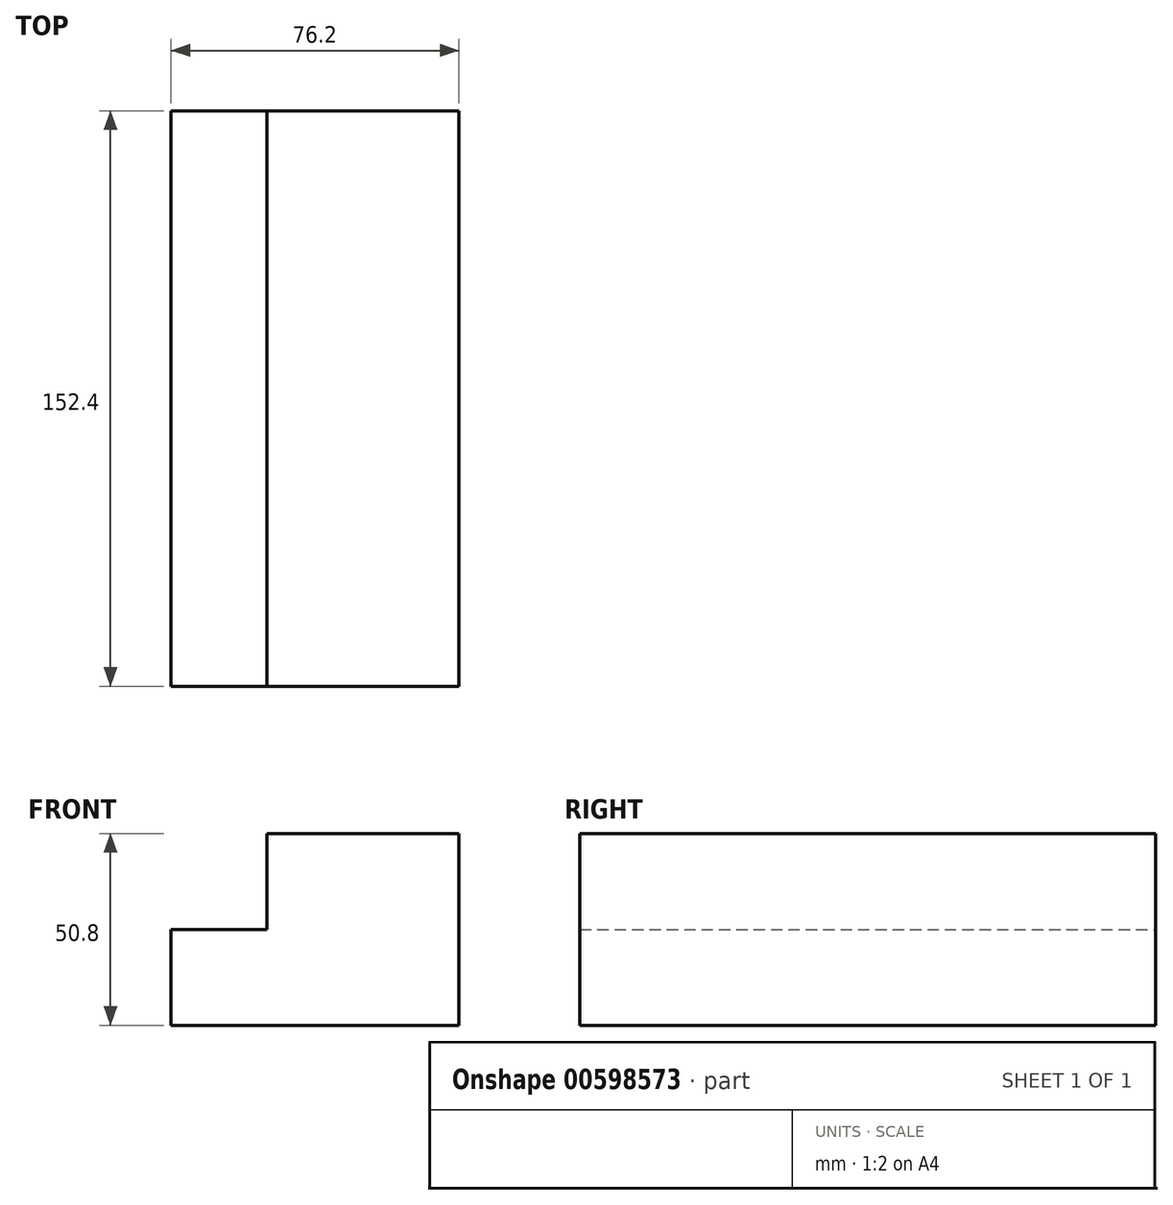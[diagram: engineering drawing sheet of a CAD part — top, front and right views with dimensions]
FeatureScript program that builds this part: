
annotation { "Feature Type Name" : "Feature", "Feature Type Description" : "" }
export const myFeature = defineFeature(function(context is Context, id is Id, definition is map)
    precondition{}
    {
        {
            var Q0;
            Q0=qCreatedBy(makeId("Front.planeOp"),FACE);
            var sketch = newSketch(context, id + "F0", { "sketchPlane" : qUnion([Q0])});
            skLineSegment(sketch, "E0", {"start": v(0, 0) * mm, "end": v(0, 50.8) * mm});
            skLineSegment(sketch, "E1", {"start": v(0, 50.8) * mm, "end": v(-50.8, 50.8) * mm});
            skLineSegment(sketch, "E2", {"start": v(0, 0) * mm, "end": v(-76.2, 0) * mm});
            skLineSegment(sketch, "E3", {"start": v(-76.2, 0) * mm, "end": v(-76.2, 25.4) * mm});
            skLineSegment(sketch, "E4", {"start": v(-76.2, 25.4) * mm, "end": v(-50.8, 25.4) * mm});
            skLineSegment(sketch, "E5", {"start": v(-50.8, 25.4) * mm, "end": v(-50.8, 50.8) * mm});
            skSolve(sketch);
        }
        {
            var Q0;
            Q0 = qSketchRegion(id + "F0", true);
            extrude(context, id + "F1", {"entities" : qUnion([Q0]), "depth" : 152.4 * mm, "offsetDistance" : 25.4 * mm});
        }
    });
